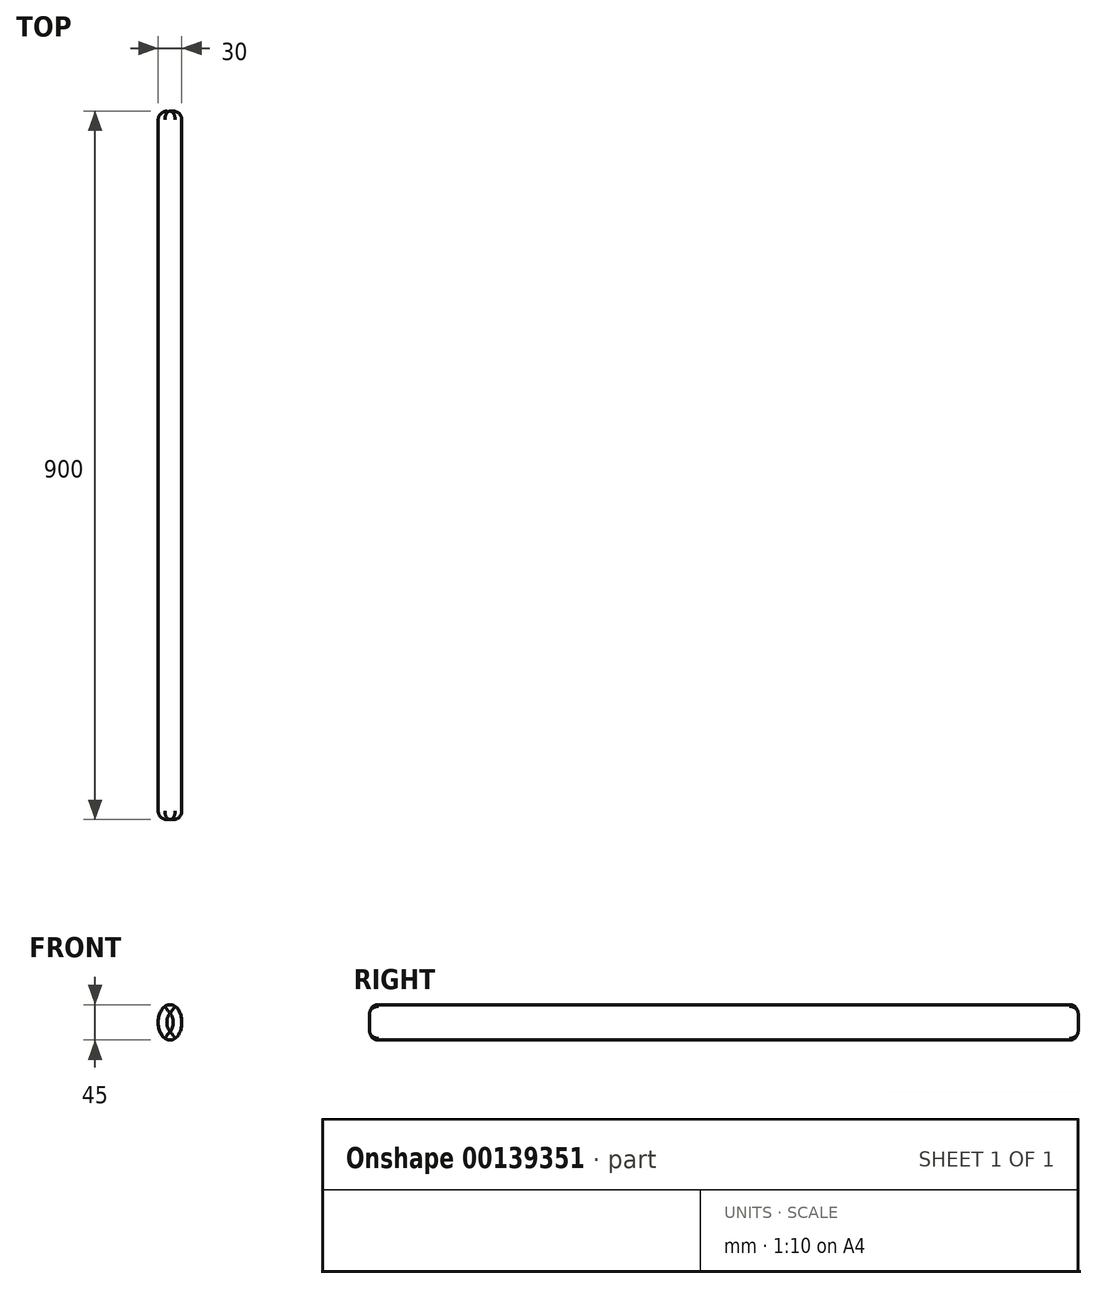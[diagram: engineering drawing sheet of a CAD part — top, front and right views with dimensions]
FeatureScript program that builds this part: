
annotation { "Feature Type Name" : "Feature", "Feature Type Description" : "" }
export const myFeature = defineFeature(function(context is Context, id is Id, definition is map)
    precondition{}
    {
        {
            var Q0;
            Q0=qCreatedBy(makeId("Front.planeOp"),FACE);
            var sketch = newSketch(context, id + "F0", { "sketchPlane" : qUnion([Q0])});
            skLineSegment(sketch, "E0", {"start": v(0, 0) * mm, "end": v(0, 45) * mm});
            skEllipse(sketch, "E1", {"center": v(0, 22.5) * mm, "majorRadius": 22.5 * mm, "minorRadius": 15 * mm, "majorAxis": v(0, -1)});
            skLineSegment(sketch, "E2", {"start": v(0, 22.5) * mm, "end": v(15, 22.5) * mm});
            skSolve(sketch);
        }
        {
            var Q0;
            Q0=makeQuery(id+"F0.imprint","IMPRINT",FACE,{"disambiguationData":[TD([[makeQuery(id+"F0.imprint","IMPRINT",EDGE,{"derivedFrom":sQuery(id+"F0.wireOp",EDGE,"E0")}),1.0]])]});
            var Q1;
            Q1=makeQuery(id+"F0.imprint","IMPRINT",FACE,{"disambiguationData":[TD([[makeQuery(id+"F0.imprint","IMPRINT",EDGE,{"derivedFrom":sQuery(id+"F0.wireOp",EDGE,"E0")}),-1.0]])]});
            extrude(context, id + "F1", {"entities" : qUnion([Q0, Q1]), "depth" : 900 * mm});
        }
        {
            var Q0;
            Q0=makeQuery(id+"F1.opExtrude","CAP_EDGE",EDGE,{"disambiguationData":[OSD([sQuery(id+"F0.wireOp",EDGE,"l9EuCbVv-2DWD-CaYj-4VoY-RX4wOJB0O2Jx")])],"isStart":true});
            var Q1;
            Q1=makeQuery(id+"F1.opExtrude","CAP_EDGE",EDGE,{"disambiguationData":[OSD([sQuery(id+"F0.wireOp",EDGE,"64ebctOr-D7YG-8Mqt-Afzc-HaQo43nXPG3C")])],"isStart":true});
            var Q2;
            {var subQ0=sQuery(id+"F0.wireOp",EDGE,"64ebctOr-D7YG-8Mqt-Afzc-HaQo43nXPG3C");var subQ1=sQuery(id+"F0.wireOp",EDGE,"l9EuCbVv-2DWD-CaYj-4VoY-RX4wOJB0O2Jx");var subQ2=sQuery(id+"F0.wireOp",EDGE,"E0");Q2=makeQuery(id+"FSNTzi0Sil4Btze_1.opFillet","BLEND_EDGE",EDGE,{"blendedFrom":[makeQuery(id+"F1.opExtrude","SWEPT_EDGE",EDGE,{"disambiguationData":[OSD([subQ2,subQ1,subQ0]),TDD([makeQuery(id+"F0.imprint","INTERSECT",VERTEX,{"disambiguationData":[OD(0.0)],"derivedFrom":[subQ2,subQ1,subQ0]})])]}),makeQuery(id+"F1.opExtrude","CAP_FACE",FACE,{"disambiguationData":[OSD([subQ1,subQ0])],"isStart":true})],"blendedInto":[makeQuery(id+"F1.opExtrude","CAP_FACE",FACE,{"disambiguationData":[OSD([subQ1,subQ0])],"isStart":true})]});}
            var Q3;
            {var subQ0=sQuery(id+"F0.wireOp",EDGE,"64ebctOr-D7YG-8Mqt-Afzc-HaQo43nXPG3C");var subQ1=sQuery(id+"F0.wireOp",EDGE,"l9EuCbVv-2DWD-CaYj-4VoY-RX4wOJB0O2Jx");var subQ2=sQuery(id+"F0.wireOp",EDGE,"E0");Q3=makeQuery(id+"FSNTzi0Sil4Btze_1.opFillet","BLEND_EDGE",EDGE,{"blendedFrom":[makeQuery(id+"F1.opExtrude","SWEPT_EDGE",EDGE,{"disambiguationData":[OSD([subQ2,subQ1,subQ0]),TDD([makeQuery(id+"F0.imprint","INTERSECT",VERTEX,{"disambiguationData":[OD(1.0)],"derivedFrom":[subQ2,subQ1,subQ0]})])]}),makeQuery(id+"F1.opExtrude","CAP_FACE",FACE,{"disambiguationData":[OSD([subQ1,subQ0])],"isStart":true})],"blendedInto":[makeQuery(id+"F1.opExtrude","CAP_FACE",FACE,{"disambiguationData":[OSD([subQ1,subQ0])],"isStart":true})]});}
            var Q4;
            Q4=makeQuery(id+"F1.opExtrude","CAP_EDGE",EDGE,{"disambiguationData":[OSD([sQuery(id+"F0.wireOp",EDGE,"l9EuCbVv-2DWD-CaYj-4VoY-RX4wOJB0O2Jx")])],"isStart":false});
            var Q5;
            {var subQ0=sQuery(id+"F0.wireOp",EDGE,"64ebctOr-D7YG-8Mqt-Afzc-HaQo43nXPG3C");var subQ1=sQuery(id+"F0.wireOp",EDGE,"l9EuCbVv-2DWD-CaYj-4VoY-RX4wOJB0O2Jx");var subQ2=sQuery(id+"F0.wireOp",EDGE,"E0");Q5=makeQuery(id+"FSNTzi0Sil4Btze_1.opFillet","BLEND_EDGE",EDGE,{"blendedFrom":[makeQuery(id+"F1.opExtrude","SWEPT_EDGE",EDGE,{"disambiguationData":[OSD([subQ2,subQ1,subQ0]),TDD([makeQuery(id+"F0.imprint","INTERSECT",VERTEX,{"disambiguationData":[OD(0.0)],"derivedFrom":[subQ2,subQ1,subQ0]})])]}),makeQuery(id+"F1.opExtrude","CAP_FACE",FACE,{"disambiguationData":[OSD([subQ1,subQ0])],"isStart":false})],"blendedInto":[makeQuery(id+"F1.opExtrude","CAP_FACE",FACE,{"disambiguationData":[OSD([subQ1,subQ0])],"isStart":false})]});}
            var Q6;
            Q6=makeQuery(id+"F1.opExtrude","CAP_EDGE",EDGE,{"disambiguationData":[OSD([sQuery(id+"F0.wireOp",EDGE,"64ebctOr-D7YG-8Mqt-Afzc-HaQo43nXPG3C")])],"isStart":false});
            var Q7;
            {var subQ0=sQuery(id+"F0.wireOp",EDGE,"64ebctOr-D7YG-8Mqt-Afzc-HaQo43nXPG3C");var subQ1=sQuery(id+"F0.wireOp",EDGE,"l9EuCbVv-2DWD-CaYj-4VoY-RX4wOJB0O2Jx");var subQ2=sQuery(id+"F0.wireOp",EDGE,"E0");Q7=makeQuery(id+"FSNTzi0Sil4Btze_1.opFillet","BLEND_EDGE",EDGE,{"blendedFrom":[makeQuery(id+"F1.opExtrude","SWEPT_EDGE",EDGE,{"disambiguationData":[OSD([subQ2,subQ1,subQ0]),TDD([makeQuery(id+"F0.imprint","INTERSECT",VERTEX,{"disambiguationData":[OD(1.0)],"derivedFrom":[subQ2,subQ1,subQ0]})])]}),makeQuery(id+"F1.opExtrude","CAP_FACE",FACE,{"disambiguationData":[OSD([subQ1,subQ0])],"isStart":false})],"blendedInto":[makeQuery(id+"F1.opExtrude","CAP_FACE",FACE,{"disambiguationData":[OSD([subQ1,subQ0])],"isStart":false})]});}
            var Q8;
            Q8=makeQuery(id+"F1.opExtrude","CAP_EDGE",EDGE,{"disambiguationData":[OSD([sQuery(id+"F0.wireOp",EDGE,"E1")])],"isStart":false});
            var Q9;
            Q9=makeQuery(id+"F1.opExtrude","CAP_EDGE",EDGE,{"disambiguationData":[OSD([sQuery(id+"F0.wireOp",EDGE,"E1")])],"isStart":true});
            fillet(context, id + "F2", {"entities" : qUnion([Q0, Q1, Q2, Q3, Q4, Q5, Q6, Q7, Q8, Q9]), "radius" : 11 * mm, "tangentPropagation" : true, "allowEdgeOverflow" : false});
        }
    });
